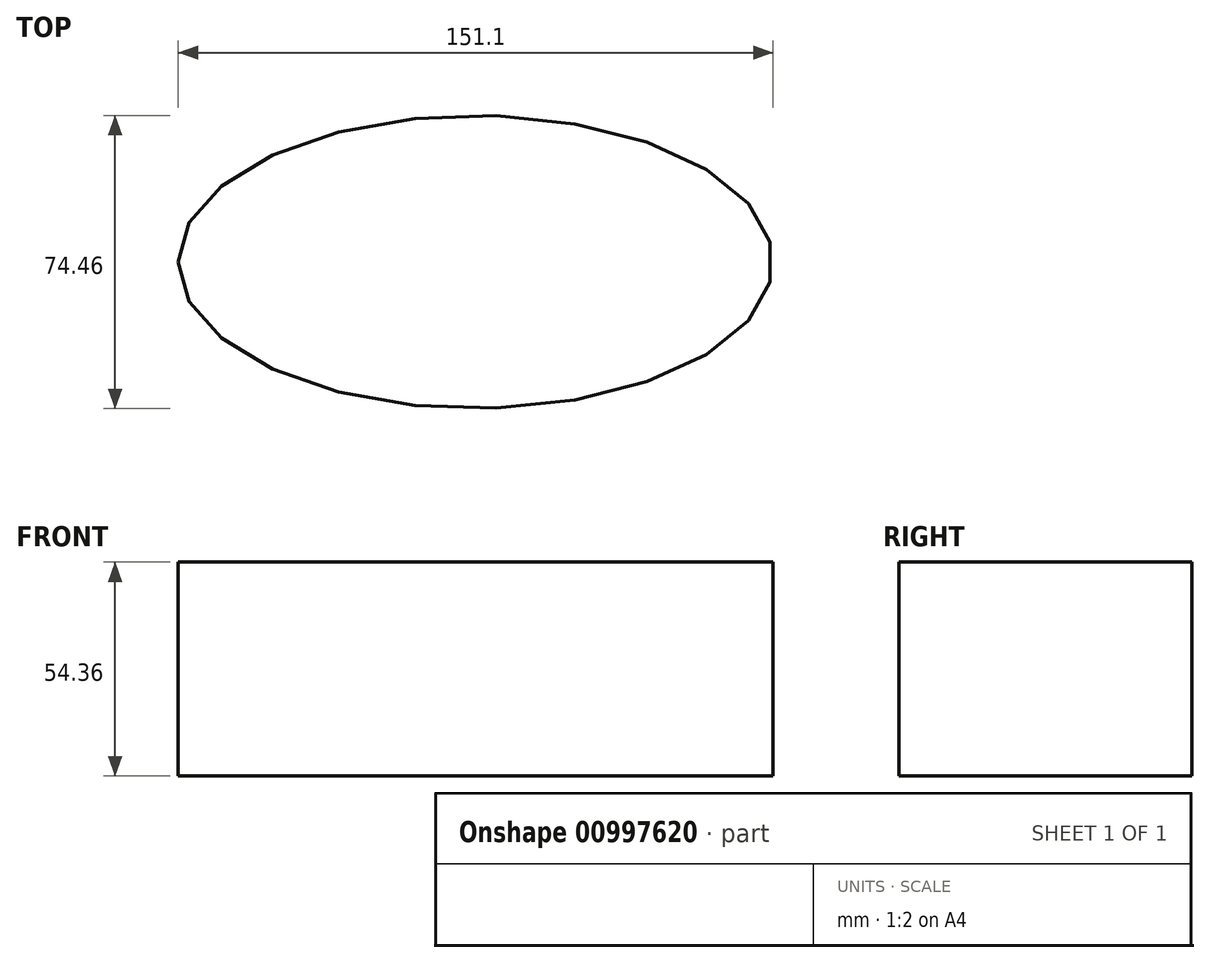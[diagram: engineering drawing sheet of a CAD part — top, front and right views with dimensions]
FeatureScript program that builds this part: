
annotation { "Feature Type Name" : "Feature", "Feature Type Description" : "" }
export const myFeature = defineFeature(function(context is Context, id is Id, definition is map)
    precondition{}
    {
        {
            var Q0;
            Q0=qCreatedBy(makeId("Top.planeOp"),FACE);
            var sketch = newSketch(context, id + "F0", { "sketchPlane" : qUnion([Q0])});
            skEllipse(sketch, "E0", {"center": v(0, 0) * mm, "majorRadius": 75.55 * mm, "minorRadius": 37.23 * mm, "majorAxis": v(-1, 0)});
            skSolve(sketch);
        }
        {
            var Q0;
            Q0=makeQuery(id+"F0.imprint","IMPRINT",FACE,{"disambiguationData":[TD([[makeQuery(id+"F0.imprint","IMPRINT",EDGE,{"derivedFrom":sQuery(id+"F0.wireOp",EDGE,"E0")}),1.0]])]});
            extrude(context, id + "F1", {"entities" : qUnion([Q0]), "depth" : 54.36 * mm, "offsetDistance" : 25.4 * mm});
        }
    });
